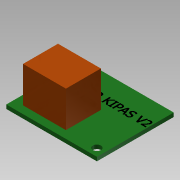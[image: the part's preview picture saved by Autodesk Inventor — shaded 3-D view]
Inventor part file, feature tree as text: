
AUTODESK INVENTOR PART (.ipt)
format: ipt  version: 2015 SP1 (Build 190203100, 203)  size: 100,352 bytes
history: native  units: mm
features: sketch x2, extrude x2
ambient origin geometry x8: Origin, YZ Plane, XZ Plane, XY Plane, X Axis, Y Axis, Z Axis, Center Point
bodies: Solid1 (feature_tree)
feature tree (4):
  sketch  "Sketch1"  dims[d0=39.751mm d1=33.655mm]
  extrude  "Extrusion1"  Depth=33.655mm
  extrude  "Extrusion2"  Depth=17.44mm
  sketch  "Sketch2"  dims[d2=3.5mm d3=3.5mm d4=3.429mm d5=3.429mm d6=3.429mm d7=3.429mm d8=18.79mm d9=15.32mm d10=24.243896mm d11=24.243896mm d12=1.7mm d13=0.0mm d14=17.44mm d15=0.0mm]
